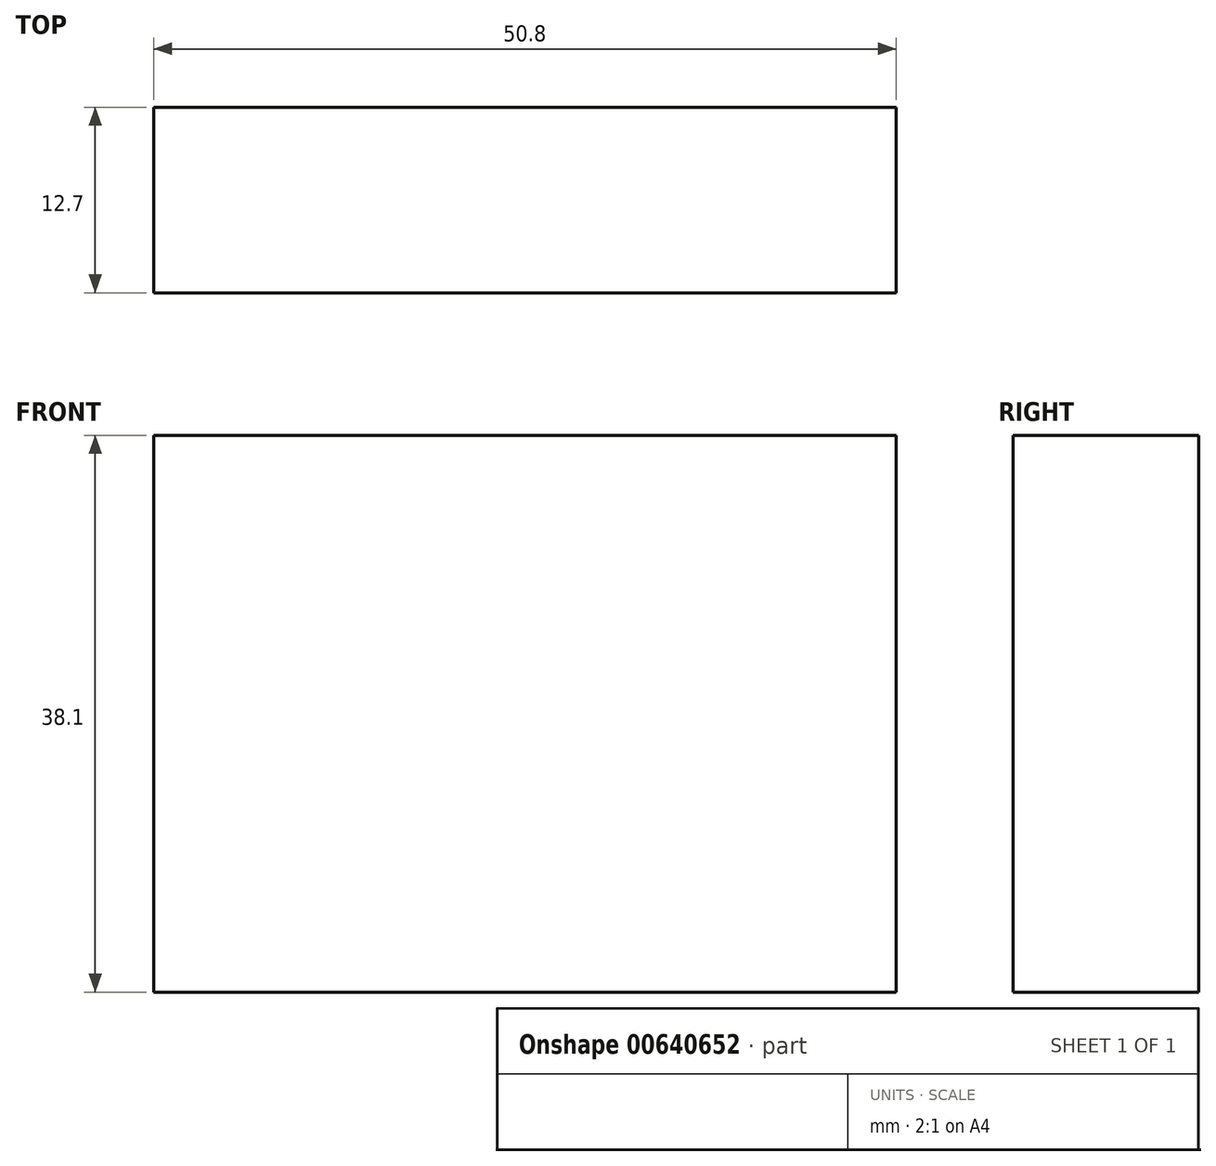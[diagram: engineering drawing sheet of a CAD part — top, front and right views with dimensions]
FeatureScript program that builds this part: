
annotation { "Feature Type Name" : "Feature", "Feature Type Description" : "" }
export const myFeature = defineFeature(function(context is Context, id is Id, definition is map)
    precondition{}
    {
        {
            var Q0;
            Q0=qCreatedBy(makeId("Front.planeOp"),FACE);
            var sketch = newSketch(context, id + "F0", { "sketchPlane" : qUnion([Q0])});
            skLineSegment(sketch, "E0.bottom", {"start": v(-68.06, 60.1) * mm, "end": v(-17.26, 60.1) * mm});
            skLineSegment(sketch, "E0.top", {"start": v(-68.06, 22) * mm, "end": v(-17.26, 22) * mm});
            skLineSegment(sketch, "E0.left", {"start": v(-68.06, 60.1) * mm, "end": v(-68.06, 22) * mm});
            skLineSegment(sketch, "E0.right", {"start": v(-17.26, 60.1) * mm, "end": v(-17.26, 22) * mm});
            skSolve(sketch);
        }
        {
            var Q0;
            Q0=makeQuery(id+"F0.imprint","IMPRINT",FACE,{"disambiguationData":[TD([[makeQuery(id+"F0.imprint","IMPRINT",EDGE,{"derivedFrom":sQuery(id+"F0.wireOp",EDGE,"E0.bottom")}),-1.0]])]});
            extrude(context, id + "F1", {"entities" : qUnion([Q0]), "depth" : 12.7 * mm, "offsetDistance" : 25.4 * mm});
        }
    });
